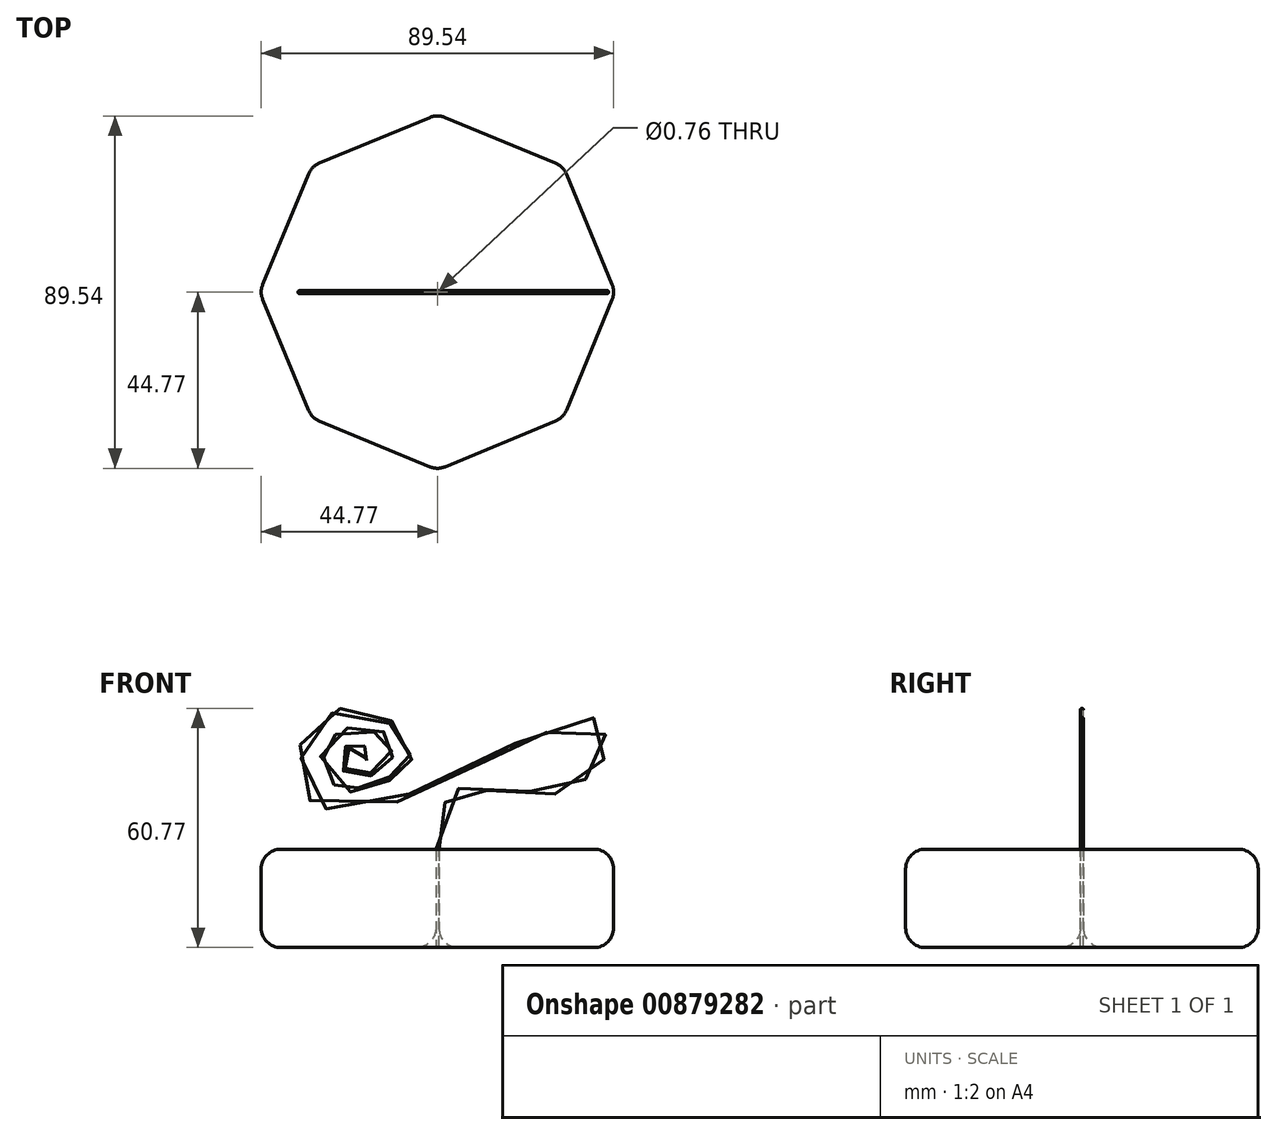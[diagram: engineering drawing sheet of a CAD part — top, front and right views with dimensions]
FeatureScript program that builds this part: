
annotation { "Feature Type Name" : "Feature", "Feature Type Description" : "" }
export const myFeature = defineFeature(function(context is Context, id is Id, definition is map)
    precondition{}
    {
        {
            var Q0;
            Q0=qCreatedBy(makeId("Top.planeOp"),FACE);
            var sketch = newSketch(context, id + "F0", { "sketchPlane" : qUnion([Q0])});
            skCircle(sketch, "E0.cCircle", {"center": v(0, 0) * mm, "radius": 45.18 * mm, "construction": true});
            skLineSegment(sketch, "E0.0", {"start": v(0, -45.18) * mm, "end": v(-31.95, -31.95) * mm});
            skLineSegment(sketch, "E0.1", {"start": v(-31.95, -31.95) * mm, "end": v(-45.18, 0) * mm});
            skLineSegment(sketch, "E0.2", {"start": v(-45.18, 0) * mm, "end": v(-31.95, 31.95) * mm});
            skLineSegment(sketch, "E0.3", {"start": v(-31.95, 31.95) * mm, "end": v(0, 45.18) * mm});
            skLineSegment(sketch, "E0.4", {"start": v(0, 45.18) * mm, "end": v(31.95, 31.95) * mm});
            skLineSegment(sketch, "E0.5", {"start": v(31.95, 31.95) * mm, "end": v(45.18, 0) * mm});
            skLineSegment(sketch, "E0.6", {"start": v(45.18, 0) * mm, "end": v(31.95, -31.95) * mm});
            skLineSegment(sketch, "E0.7", {"start": v(31.95, -31.95) * mm, "end": v(0, -45.18) * mm});
            skCircle(sketch, "E1", {"center": v(0, 0) * mm, "radius": 0.38 * mm});
            skSolve(sketch);
        }
        {
            var Q0;
            Q0 = qSketchRegion(id + "F0", true);
            extrude(context, id + "F1", {"entities" : qUnion([Q0]), "depth" : 25 * mm, "offsetDistance" : 25 * mm});
        }
        {
            var Q0;
            Q0=makeQuery(id+"F1.opExtrude","CAP_EDGE",EDGE,{"disambiguationData":[OSD([sQuery(id+"F0.wireOp",EDGE,"E0.0")])],"isStart":false});
            var Q1;
            Q1=makeQuery(id+"F1.opExtrude","CAP_EDGE",EDGE,{"disambiguationData":[OSD([sQuery(id+"F0.wireOp",EDGE,"E0.1")])],"isStart":false});
            var Q2;
            Q2=makeQuery(id+"F1.opExtrude","CAP_EDGE",EDGE,{"disambiguationData":[OSD([sQuery(id+"F0.wireOp",EDGE,"E0.2")])],"isStart":false});
            var Q3;
            Q3=makeQuery(id+"F1.opExtrude","CAP_EDGE",EDGE,{"disambiguationData":[OSD([sQuery(id+"F0.wireOp",EDGE,"E0.3")])],"isStart":false});
            var Q4;
            Q4=makeQuery(id+"F1.opExtrude","CAP_EDGE",EDGE,{"disambiguationData":[OSD([sQuery(id+"F0.wireOp",EDGE,"E0.4")])],"isStart":false});
            var Q5;
            Q5=makeQuery(id+"F1.opExtrude","CAP_EDGE",EDGE,{"disambiguationData":[OSD([sQuery(id+"F0.wireOp",EDGE,"E0.5")])],"isStart":false});
            var Q6;
            Q6=makeQuery(id+"F1.opExtrude","CAP_EDGE",EDGE,{"disambiguationData":[OSD([sQuery(id+"F0.wireOp",EDGE,"E0.6")])],"isStart":false});
            var Q7;
            Q7=makeQuery(id+"F1.opExtrude","CAP_EDGE",EDGE,{"disambiguationData":[OSD([sQuery(id+"F0.wireOp",EDGE,"E0.7")])],"isStart":false});
            var Q8;
            Q8=makeQuery(id+"F1.opExtrude","CAP_FACE",FACE,{"disambiguationData":[OSD([sQuery(id+"F0.wireOp",EDGE,"E0.0"),sQuery(id+"F0.wireOp",EDGE,"E0.1"),sQuery(id+"F0.wireOp",EDGE,"E0.2"),sQuery(id+"F0.wireOp",EDGE,"E0.3"),sQuery(id+"F0.wireOp",EDGE,"E0.4"),sQuery(id+"F0.wireOp",EDGE,"E0.5"),sQuery(id+"F0.wireOp",EDGE,"E0.6"),sQuery(id+"F0.wireOp",EDGE,"E0.7")])],"isStart":true});
            var Q9;
            Q9=makeQuery(id+"F1.opExtrude","SWEPT_EDGE",EDGE,{"disambiguationData":[OSD([sQuery(id+"F0.wireOp",EDGE,"E0.6"),sQuery(id+"F0.wireOp",EDGE,"E0.7")])]});
            var Q10;
            Q10=makeQuery(id+"F1.opExtrude","SWEPT_FACE",FACE,{"disambiguationData":[OSD([sQuery(id+"F0.wireOp",EDGE,"E0.7")])]});
            var Q11;
            Q11=makeQuery(id+"F1.opExtrude","SWEPT_EDGE",EDGE,{"disambiguationData":[OSD([sQuery(id+"F0.wireOp",EDGE,"E0.5"),sQuery(id+"F0.wireOp",EDGE,"E0.6")])]});
            var Q12;
            Q12=makeQuery(id+"F1.opExtrude","SWEPT_EDGE",EDGE,{"disambiguationData":[OSD([sQuery(id+"F0.wireOp",EDGE,"E0.4"),sQuery(id+"F0.wireOp",EDGE,"E0.5")])]});
            var Q13;
            Q13=makeQuery(id+"F1.opExtrude","SWEPT_EDGE",EDGE,{"disambiguationData":[OSD([sQuery(id+"F0.wireOp",EDGE,"E0.3"),sQuery(id+"F0.wireOp",EDGE,"E0.4")])]});
            var Q14;
            Q14=makeQuery(id+"F1.opExtrude","SWEPT_EDGE",EDGE,{"disambiguationData":[OSD([sQuery(id+"F0.wireOp",EDGE,"E0.2"),sQuery(id+"F0.wireOp",EDGE,"E0.3")])]});
            var Q15;
            Q15=makeQuery(id+"F1.opExtrude","SWEPT_EDGE",EDGE,{"disambiguationData":[OSD([sQuery(id+"F0.wireOp",EDGE,"E0.1"),sQuery(id+"F0.wireOp",EDGE,"E0.2")])]});
            var Q16;
            Q16=makeQuery(id+"F1.opExtrude","SWEPT_EDGE",EDGE,{"disambiguationData":[OSD([sQuery(id+"F0.wireOp",EDGE,"E0.0"),sQuery(id+"F0.wireOp",EDGE,"E0.1")])]});
            fillet(context, id + "F2", {"entities" : qUnion([Q0, Q1, Q2, Q3, Q4, Q5, Q6, Q7, Q8, Q9, Q10, Q11, Q12, Q13, Q14, Q15, Q16]), "radius" : 5 * mm, "tangentPropagation" : true, "allowEdgeOverflow" : false});
        }
        {
            var Q0;
            Q0=qCreatedBy(makeId("Front.planeOp"),FACE);
            var sketch = newSketch(context, id + "F3", { "sketchPlane" : qUnion([Q0])});
            skFitSpline(sketch, "E2", {"points": [v(0, 0) * mm, v(0, 24.67) * mm, v(4.55, 39.76) * mm, v(36.47, 41.5) * mm, v(40.54, 57.76) * mm, v(-27.96, 34.73) * mm, v(-30.47, 58.14) * mm, v(-7.45, 53.5) * mm, v(-8.61, 45.37) * mm, v(-16.35, 41.3) * mm, v(-24.09, 39.96) * mm, v(-27.96, 43.05) * mm, v(-28.93, 51.56) * mm, v(-22.54, 55.43) * mm, v(-11.32, 52.53) * mm, v(-14.22, 45.57) * mm, v(-20.8, 43.83) * mm, v(-24.86, 47.3) * mm, v(-20.62, 51.48) * mm, v(-18.17, 47.95) * mm], "startDerivative": vector(1.13, 356.98) * mm, "endDerivative": vector(-239.27, -111.74) * mm});
            skSolve(sketch);
        }
        {
            var Q0;
            Q0=makeQuery(id+"F0.imprint","IMPRINT",FACE,{"disambiguationData":[TD([[makeQuery(id+"F0.imprint","IMPRINT",EDGE,{"derivedFrom":sQuery(id+"F0.wireOp",EDGE,"E1")}),1.0]])]});
            var Q1;
            Q1=sQuery(id+"F3.wireOp",EDGE,"E2");
            sweep(context, id + "F4", {"profiles" : qUnion([Q0]), "path" : qUnion([Q1])});
        }
    });
